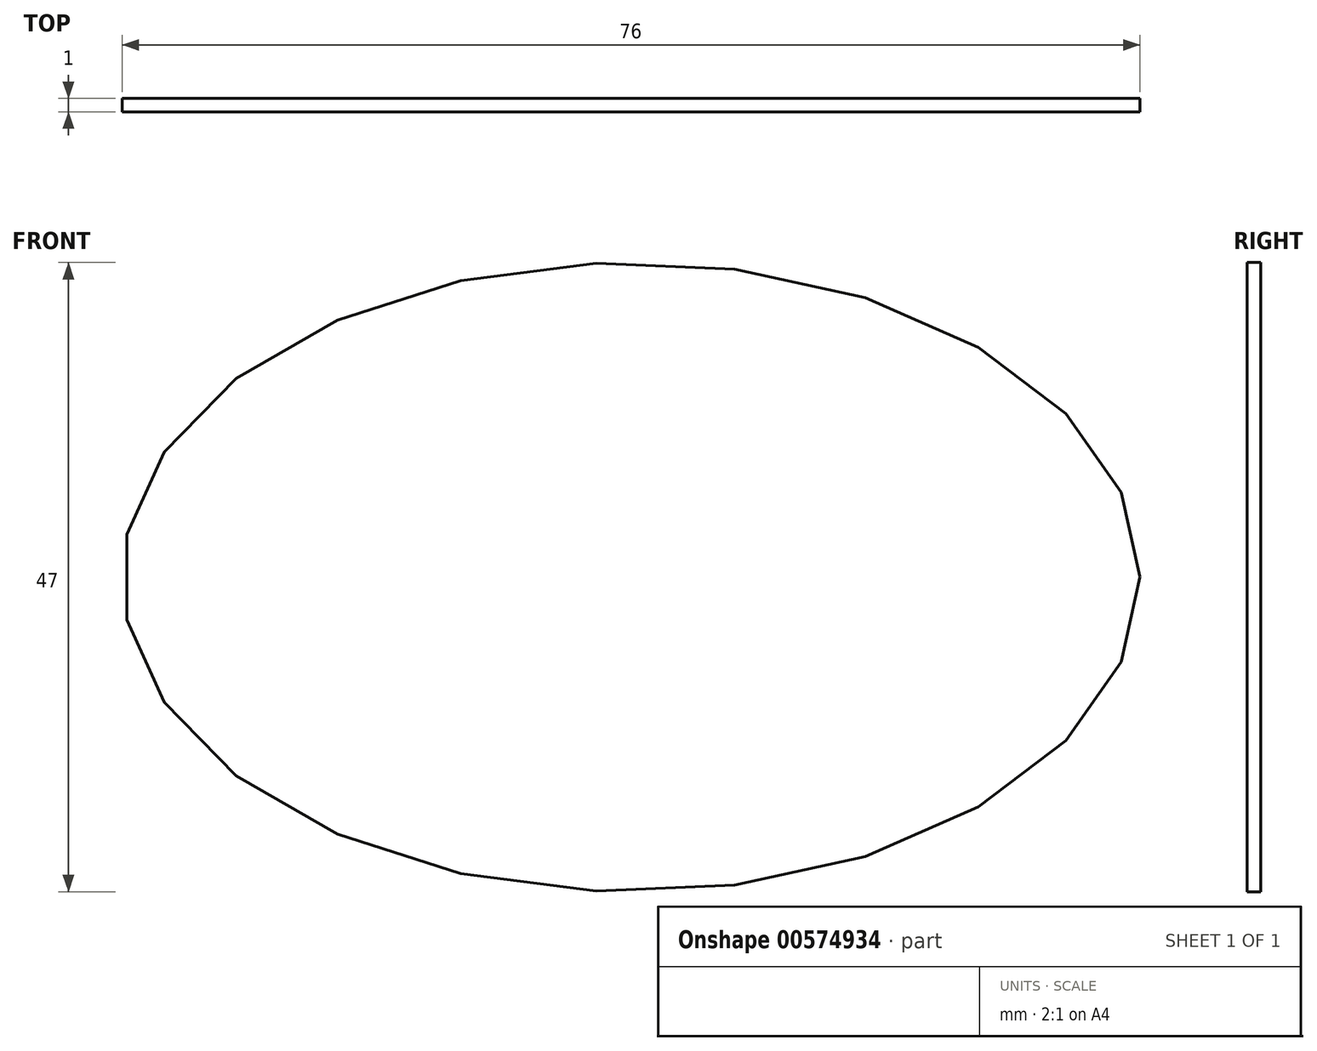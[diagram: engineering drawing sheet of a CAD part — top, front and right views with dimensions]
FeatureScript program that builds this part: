
annotation { "Feature Type Name" : "Feature", "Feature Type Description" : "" }
export const myFeature = defineFeature(function(context is Context, id is Id, definition is map)
    precondition{}
    {
        {
            var Q0;
            Q0=qCreatedBy(makeId("Front.planeOp"),FACE);
            var sketch = newSketch(context, id + "F0", { "sketchPlane" : qUnion([Q0])});
            skEllipse(sketch, "E0.0", {"center": v(0, 0) * mm, "majorRadius": 38 * mm, "minorRadius": 23.5 * mm, "majorAxis": v(1, 0)});
            skFitSpline(sketch, "E1.0", {"points": [v(37.37, -1.12) * mm, v(37.41, 0) * mm, v(37.37, 1.12) * mm, v(37.2, 2.6) * mm, v(36.75, 4.43) * mm, v(35.88, 6.58) * mm, v(34.66, 8.67) * mm, v(33.12, 10.69) * mm, v(31.26, 12.62) * mm, v(29.45, 14.13) * mm, v(27.84, 15.28) * mm, v(26.57, 16.11) * mm, v(25.22, 16.9) * mm, v(23.35, 17.9) * mm, v(20.89, 19.03) * mm, v(17.73, 20.2) * mm, v(14.42, 21.16) * mm, v(10.96, 21.93) * mm, v(7.39, 22.48) * mm, v(4.34, 22.77) * mm, v(1.87, 22.88) * mm, v(0, 22.9) * mm, v(-1.87, 22.88) * mm, v(-4.34, 22.77) * mm, v(-7.39, 22.48) * mm, v(-10.96, 21.93) * mm, v(-14.42, 21.16) * mm, v(-17.73, 20.2) * mm, v(-20.89, 19.03) * mm, v(-23.35, 17.9) * mm, v(-25.22, 16.9) * mm, v(-26.57, 16.11) * mm, v(-27.84, 15.28) * mm, v(-29.45, 14.13) * mm, v(-31.26, 12.62) * mm, v(-33.12, 10.69) * mm, v(-34.66, 8.67) * mm, v(-35.88, 6.58) * mm, v(-36.75, 4.43) * mm, v(-37.2, 2.6) * mm, v(-37.37, 1.12) * mm, v(-37.42, 0) * mm, v(-37.37, -1.12) * mm, v(-37.2, -2.6) * mm, v(-36.75, -4.43) * mm, v(-35.88, -6.58) * mm, v(-34.66, -8.67) * mm, v(-33.12, -10.69) * mm, v(-31.26, -12.62) * mm, v(-29.45, -14.13) * mm, v(-27.84, -15.28) * mm, v(-26.57, -16.11) * mm, v(-25.22, -16.9) * mm, v(-23.35, -17.9) * mm, v(-20.89, -19.03) * mm, v(-17.73, -20.2) * mm, v(-14.42, -21.16) * mm, v(-10.96, -21.93) * mm, v(-7.39, -22.48) * mm, v(-4.34, -22.77) * mm, v(-1.87, -22.88) * mm, v(0, -22.9) * mm, v(1.87, -22.88) * mm, v(4.34, -22.77) * mm, v(7.39, -22.48) * mm, v(10.96, -21.93) * mm, v(14.42, -21.16) * mm, v(17.73, -20.2) * mm, v(20.89, -19.03) * mm, v(23.35, -17.9) * mm, v(25.22, -16.9) * mm, v(26.57, -16.11) * mm, v(27.84, -15.28) * mm, v(29.45, -14.13) * mm, v(31.26, -12.62) * mm, v(33.12, -10.69) * mm, v(34.66, -8.67) * mm, v(35.88, -6.58) * mm, v(36.75, -4.43) * mm, v(37.2, -2.6) * mm, v(37.37, -1.12) * mm, v(37.41, 0) * mm, v(37.37, 1.12) * mm, v(37.37, -1.12) * mm]});
            skSolve(sketch);
        }
        {
            var Q0;
            Q0 = qSketchRegion(id + "F0", true);
            var Q1;
            Q1=sQuery(id+"F0.wireOp",EDGE,"E0.0");
            var Q2;
            Q2=sQuery(id+"F0.wireOp",EDGE,"E1.0");
            extrude(context, id + "F1", {"entities" : qUnion([Q0]), "surfaceEntities" : qUnion([Q1, Q2]), "depth" : 1 * mm, "offsetDistance" : 25 * mm});
        }
    });
